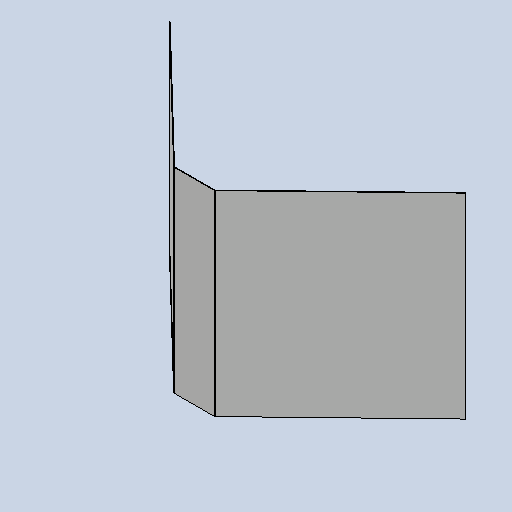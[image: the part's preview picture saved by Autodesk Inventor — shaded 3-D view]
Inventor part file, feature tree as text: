
AUTODESK INVENTOR PART (.ipt)
format: ipt  version: 2025 (Build 290162010, 162A)  size: 287,744 bytes
history: native  units: mm
features: other x4, sheet_metal_op x3, sketch x2, mirror x1
ambient origin geometry x8: Origin, YZ Plane, XZ Plane, XY Plane, X Axis, Y Axis, Z Axis, Center Point
bodies: Solid1 (feature_tree)
feature tree (10):
  sheet_metal_op  "Contour Flange1"
  mirror  "Mirror1"
  other  "Mark1"
  other  "A-Side Definition"
  sketch  "Sketch1"  dims[d7=3.0mm]
  other  "Plate1"
  sheet_metal_op  "Bend1"
  sheet_metal_op  "Corner1"
  sketch  "Sketch2"  dims[d8=3.0mm d9=1.5mm d10=6.0mm d11=3.0mm d12=980.0mm d13=3.0mm d14=3.0mm d15=12.0mm d16=3.0mm d17=3.0mm d25=6.0mm d38=6.0mm d39=3.0mm d40=3.0mm d44=3.0mm d48=742.222353mm d49=23.736478mm d50=100.0mm d51=887.0mm]
  other  "Definition1"
